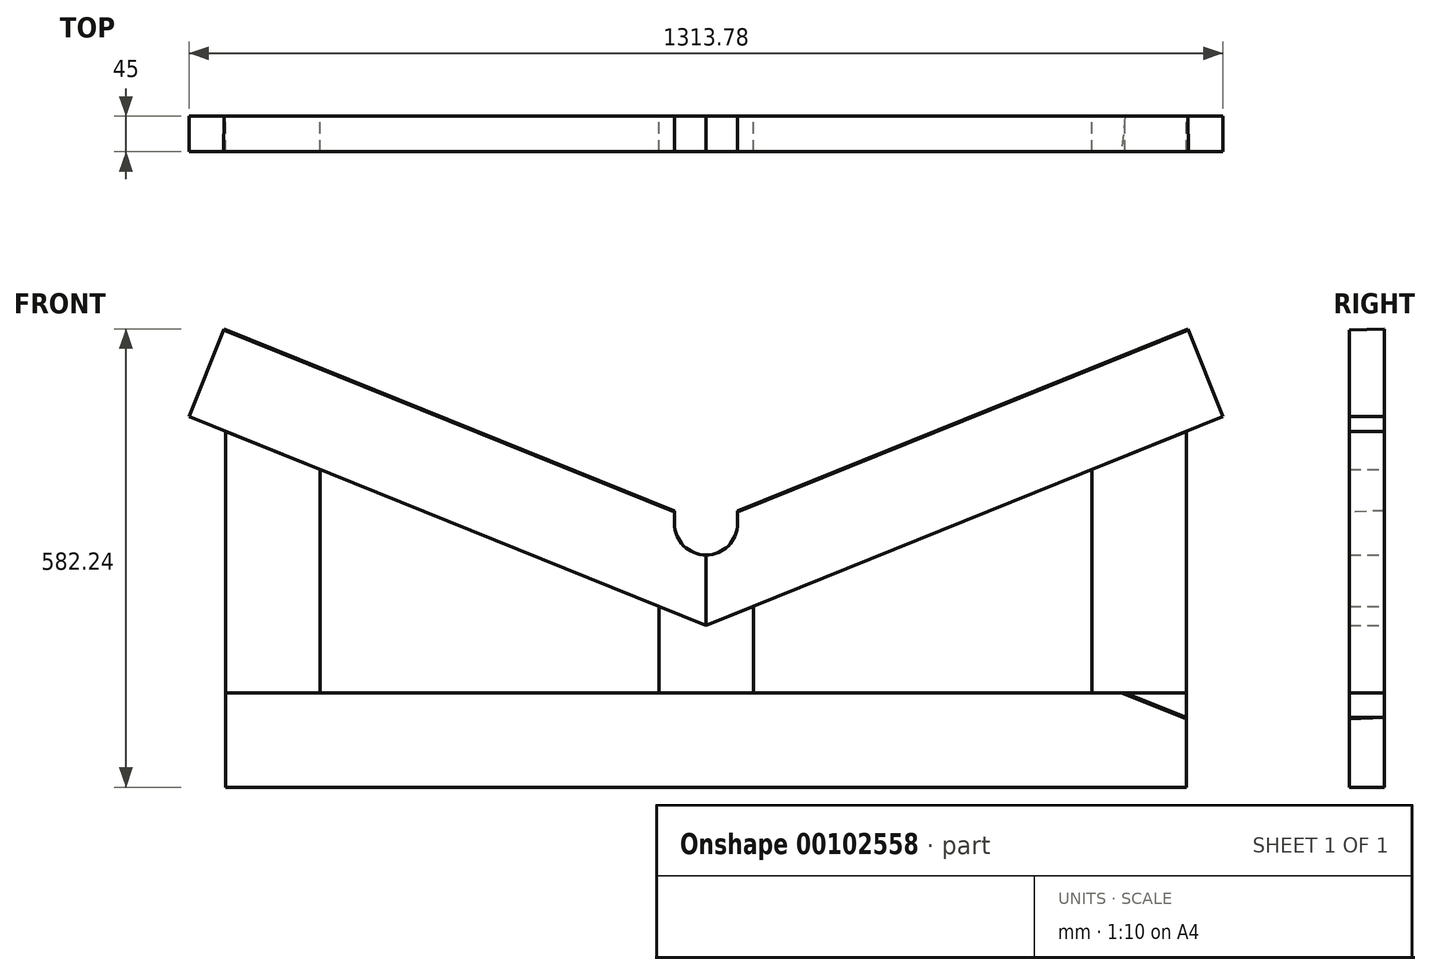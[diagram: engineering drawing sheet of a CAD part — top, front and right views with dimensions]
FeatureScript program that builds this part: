
annotation { "Feature Type Name" : "Feature", "Feature Type Description" : "" }
export const myFeature = defineFeature(function(context is Context, id is Id, definition is map)
    precondition{}
    {
        {
            var Q0;
            Q0=qCreatedBy(makeId("Front.planeOp"),FACE);
            var sketch = newSketch(context, id + "F0", { "sketchPlane" : qUnion([Q0])});
            skLineSegment(sketch, "E0.bottom", {"start": v(0, 0) * mm, "end": v(1220, 0) * mm});
            skLineSegment(sketch, "E0.top", {"start": v(0, 120) * mm, "end": v(1220, 120) * mm});
            skLineSegment(sketch, "E0.left", {"start": v(0, 0) * mm, "end": v(0, 120) * mm});
            skLineSegment(sketch, "E0.right", {"start": v(1220, 0) * mm, "end": v(1220, 120) * mm});
            skSolve(sketch);
        }
        {
            var Q0;
            Q0=makeQuery(id+"F0.imprint","IMPRINT",FACE,{"disambiguationData":[TD([[makeQuery(id+"F0.imprint","IMPRINT",EDGE,{"derivedFrom":sQuery(id+"F0.wireOp",EDGE,"E0.bottom")}),1.0]])]});
            extrude(context, id + "F1", {"entities" : qUnion([Q0]), "depth" : 45 * mm});
        }
        {
            var Q0;
            Q0=qCreatedBy(makeId("Right.planeOp"),FACE);
            cPlane(context, id + "F2", {"entities" : qUnion([Q0]), "cplaneType" : CPlaneType.OFFSET, "offset" : 610 * mm, "width" : 150 * mm, "height" : 150 * mm});
        }
        {
            var Q0;
            Q0=qCreatedBy(makeId("Front.planeOp"),FACE);
            var sketch = newSketch(context, id + "F3", { "sketchPlane" : qUnion([Q0])});
            skLineSegment(sketch, "E1", {"start": v(610, 0) * mm, "end": v(610, 335) * mm, "construction": true});
            skLineSegment(sketch, "E2", {"start": v(570, 351.16) * mm, "end": v(-1.94, 582.24) * mm});
            skLineSegment(sketch, "E3.0", {"start": v(610, 205.58) * mm, "end": v(-46.9, 470.98) * mm});
            skLineSegment(sketch, "E4", {"start": v(-1.94, 582.24) * mm, "end": v(-46.9, 470.98) * mm});
            skLineSegment(sketch, "E5", {"start": v(610, 205.58) * mm, "end": v(610, 295) * mm});
            skArc(sketch, "E6", {"start": v(570, 335) * mm, "mid": v(581.72, 306.72) * mm, "end": v(610, 295) * mm});
            skLineSegment(sketch, "E7", {"start": v(570, 335) * mm, "end": v(570, 351.16) * mm});
            skSolve(sketch);
        }
        {
            var Q0;
            Q0=makeQuery(id+"F3.imprint","IMPRINT",FACE,{"disambiguationData":[TD([[makeQuery(id+"F3.imprint","IMPRINT",EDGE,{"derivedFrom":sQuery(id+"F3.wireOp",EDGE,"E2")}),1.0]])]});
            extrude(context, id + "F4", {"entities" : qUnion([Q0]), "depth" : 45 * mm});
        }
        {
            var Q0;
            Q0=makeQuery(id+"F4.opExtrude","SWEPT_FACE",FACE,{"disambiguationData":[OSD([sQuery(id+"F3.wireOp",EDGE,"E4")])]});
            var sketch = newSketch(context, id + "F5", { "sketchPlane" : qUnion([Q0])});
            skLineSegment(sketch, "E8", {"start": v(45, 539.12) * mm, "end": v(0, 539.12) * mm});
            skLineSegment(sketch, "E9", {"start": v(0, 539.12) * mm, "end": v(45, 537.55) * mm});
            skLineSegment(sketch, "E10", {"start": v(45, 537.55) * mm, "end": v(45, 539.12) * mm});
            skSolve(sketch);
        }
        {
            var Q0;
            Q0=qSketchRegion(id+"F5",true);
            extrude(context, id + "F6", {"entities" : qUnion([Q0]), "operationType" : NewBodyOperationType.REMOVE, "endBound" : BoundingType.THROUGH_ALL, "oppositeDirection" : true, "depth" : 25 * mm});
        }
        {
            var Q0;
            Q0=qCreatedBy(makeId("Front.planeOp"),FACE);
            var sketch = newSketch(context, id + "F7", { "sketchPlane" : qUnion([Q0])});
            skLineSegment(sketch, "E11", {"start": v(0, 120) * mm, "end": v(0, 452.03) * mm});
            skLineSegment(sketch, "E12.0", {"start": v(120, 120) * mm, "end": v(120, 403.55) * mm});
            skLineSegment(sketch, "E13", {"start": v(0, 452.03) * mm, "end": v(120, 403.55) * mm});
            skLineSegment(sketch, "E14", {"start": v(0, 120) * mm, "end": v(120, 120) * mm});
            skSolve(sketch);
        }
        {
            var Q0;
            Q0=makeQuery(id+"F7.imprint","IMPRINT",FACE,{"disambiguationData":[TD([[makeQuery(id+"F7.imprint","IMPRINT",EDGE,{"derivedFrom":sQuery(id+"F7.wireOp",EDGE,"E11")}),-1.0]])]});
            extrude(context, id + "F8", {"entities" : qUnion([Q0]), "depth" : 45 * mm});
        }
        {
            var Q0;
            Q0=makeQuery(id+"F4.opExtrude","SWEPT_BODY",BODY,{"disambiguationData":[OSD([sQuery(id+"F3.wireOp",EDGE,"E2"),sQuery(id+"F3.wireOp",EDGE,"E3.0"),sQuery(id+"F3.wireOp",EDGE,"E4"),sQuery(id+"F3.wireOp",EDGE,"E5")])]});
            var Q1;
            Q1=makeQuery(id+"F8.opExtrude","SWEPT_BODY",BODY,{"disambiguationData":[OSD([sQuery(id+"F7.wireOp",EDGE,"E11"),sQuery(id+"F7.wireOp",EDGE,"E12.0"),sQuery(id+"F7.wireOp",EDGE,"E13"),sQuery(id+"F7.wireOp",EDGE,"E14")])]});
            var Q2;
            Q2=qCreatedBy(id+"F2.planeOp",FACE);
            mirror(context, id + "F9", {"entities" : qUnion([Q0, Q1]), "mirrorPlane" : qUnion([Q2])});
        }
        {
            var Q0;
            Q0=qCreatedBy(makeId("Front.planeOp"),FACE);
            var sketch = newSketch(context, id + "F10", { "sketchPlane" : qUnion([Q0])});
            skLineSegment(sketch, "E15", {"start": v(610, 120) * mm, "end": v(610, 205.58) * mm, "construction": true});
            skLineSegment(sketch, "E16.0", {"start": v(670, 120) * mm, "end": v(670, 229.82) * mm});
            skLineSegment(sketch, "E17.MirrorCS", {"start": v(550, 120) * mm, "end": v(550, 229.82) * mm});
            skLineSegment(sketch, "E18", {"start": v(550, 229.82) * mm, "end": v(610, 205.58) * mm});
            skLineSegment(sketch, "E19", {"start": v(550, 120) * mm, "end": v(670, 120) * mm});
            skLineSegment(sketch, "E20", {"start": v(610, 205.58) * mm, "end": v(670, 229.82) * mm});
            skSolve(sketch);
        }
        {
            var Q0;
            Q0=qSketchRegion(id+"F10",true);
            extrude(context, id + "F11", {"entities" : qUnion([Q0]), "depth" : 45 * mm});
        }
    });
